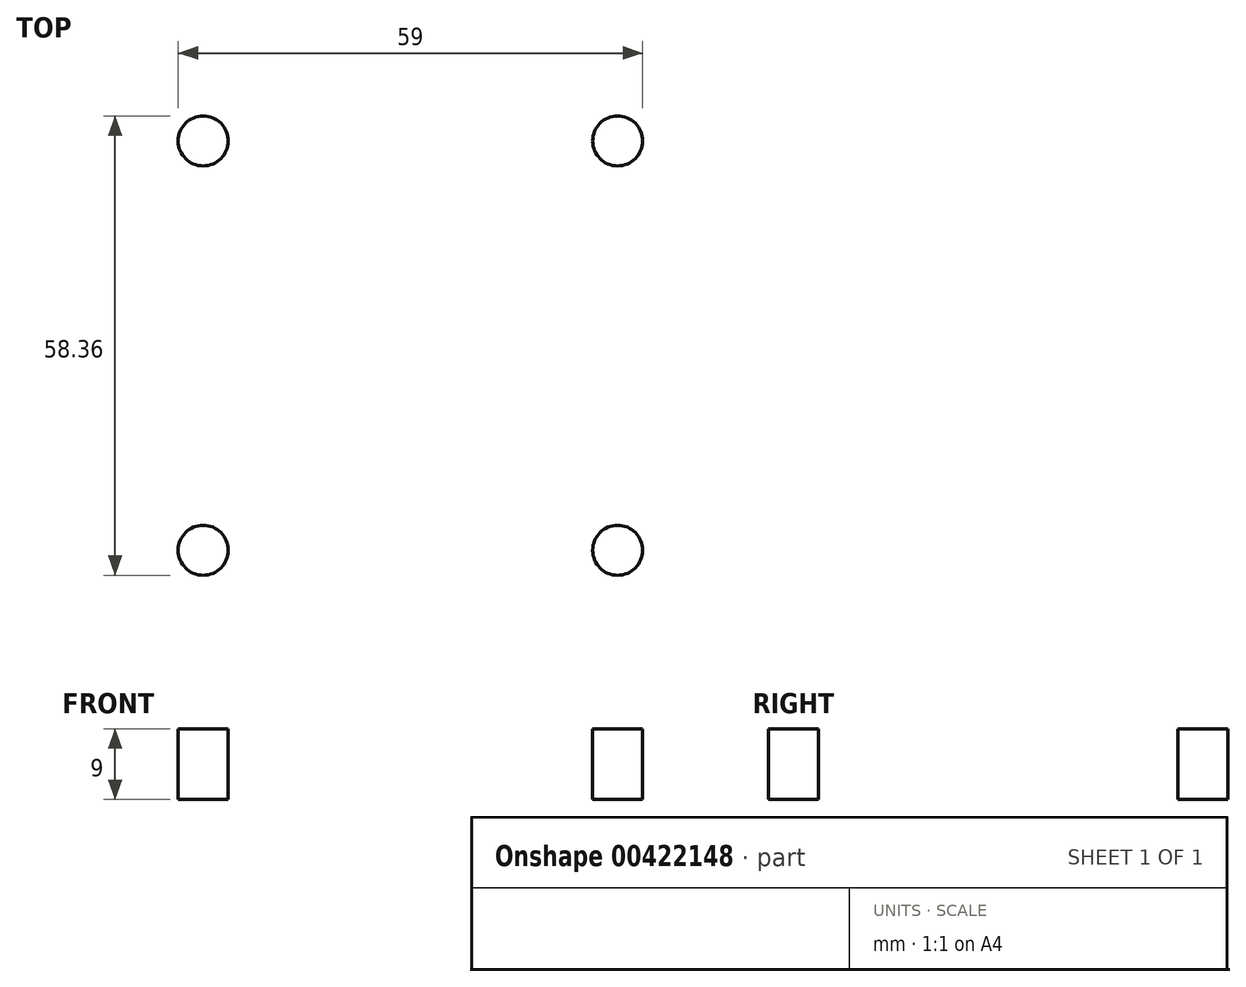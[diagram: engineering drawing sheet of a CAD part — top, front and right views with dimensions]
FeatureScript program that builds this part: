
annotation { "Feature Type Name" : "Feature", "Feature Type Description" : "" }
export const myFeature = defineFeature(function(context is Context, id is Id, definition is map)
    precondition{}
    {
        {
            var Q0;
            Q0=qCreatedBy(makeId("Top.planeOp"),FACE);
            var sketch = newSketch(context, id + "F0", { "sketchPlane" : qUnion([Q0])});
            skLineSegment(sketch, "E0", {"start": v(0, 60) * mm, "end": v(0, -60) * mm});
            skLineSegment(sketch, "E1", {"start": v(-70, 0) * mm, "end": v(70, 0) * mm});
            skLineSegment(sketch, "E2", {"start": v(-31, 37.5) * mm, "end": v(31, 37.5) * mm});
            skLineSegment(sketch, "E3", {"start": v(-31, -37.5) * mm, "end": v(31, -37.5) * mm});
            skCircle(sketch, "E4", {"center": v(-26.32, 26) * mm, "radius": 3.17 * mm});
            skCircle(sketch, "E5", {"center": v(-26.32, -26) * mm, "radius": 3.17 * mm});
            skCircle(sketch, "E6", {"center": v(26.32, -26) * mm, "radius": 3.17 * mm});
            skCircle(sketch, "E7", {"center": v(26.32, 26) * mm, "radius": 3.17 * mm});
            skCircle(sketch, "E8", {"center": v(-41, 0) * mm, "radius": 5.25 * mm});
            skCircle(sketch, "E9", {"center": v(41, 0) * mm, "radius": 5.25 * mm});
            skCircle(sketch, "E10", {"center": v(35, -11) * mm, "radius": 3.5 * mm});
            skLineSegment(sketch, "E11", {"start": v(-55, 12.5) * mm, "end": v(-55, -12.5) * mm});
            skLineSegment(sketch, "E12", {"start": v(55, 12.5) * mm, "end": v(55, -12.5) * mm});
            skCircle(sketch, "E13", {"center": v(0, 22.5) * mm, "radius": 3.17 * mm});
            skCircle(sketch, "E14", {"center": v(22.5, 0) * mm, "radius": 3.17 * mm});
            skCircle(sketch, "E15", {"center": v(0, -22.5) * mm, "radius": 3.17 * mm});
            skCircle(sketch, "E16", {"center": v(-22.5, 0) * mm, "radius": 3.17 * mm});
            skLineSegment(sketch, "E17", {"start": v(-40, 28.5) * mm, "end": v(-40, 27.5) * mm});
            skLineSegment(sketch, "E18", {"start": v(40, 28.5) * mm, "end": v(40, 27.5) * mm});
            skLineSegment(sketch, "E19", {"start": v(-40, -27.5) * mm, "end": v(-40, -28.5) * mm});
            skLineSegment(sketch, "E20", {"start": v(40, -27.5) * mm, "end": v(40, -28.5) * mm});
            skArc(sketch, "E21", {"start": v(-54, 13.5) * mm, "mid": v(-44.1, 17.6) * mm, "end": v(-40, 27.5) * mm});
            skArc(sketch, "E22", {"start": v(-40, -27.5) * mm, "mid": v(-44.1, -17.6) * mm, "end": v(-54, -13.5) * mm});
            skArc(sketch, "E23", {"start": v(54, -13.5) * mm, "mid": v(44.1, -17.6) * mm, "end": v(40, -27.5) * mm});
            skArc(sketch, "E24", {"start": v(40, 27.5) * mm, "mid": v(44.1, 17.6) * mm, "end": v(54, 13.5) * mm});
            skArc(sketch, "E25", {"start": v(-54, 13.5) * mm, "mid": v(-54.7, 13.2) * mm, "end": v(-55, 12.5) * mm});
            skArc(sketch, "E26", {"start": v(-55, -12.5) * mm, "mid": v(-54.7, -13.2) * mm, "end": v(-54, -13.5) * mm});
            skArc(sketch, "E27", {"start": v(55, 12.5) * mm, "mid": v(54.7, 13.2) * mm, "end": v(54, 13.5) * mm});
            skArc(sketch, "E28", {"start": v(54, -13.5) * mm, "mid": v(54.7, -13.2) * mm, "end": v(55, -12.5) * mm});
            skArc(sketch, "E29", {"start": v(-31, 37.5) * mm, "mid": v(-37.36, 34.86) * mm, "end": v(-40, 28.5) * mm});
            skArc(sketch, "E30", {"start": v(40, 28.5) * mm, "mid": v(37.36, 34.86) * mm, "end": v(31, 37.5) * mm});
            skArc(sketch, "E31", {"start": v(31, -37.5) * mm, "mid": v(37.36, -34.86) * mm, "end": v(40, -28.5) * mm});
            skArc(sketch, "E32", {"start": v(-40, -28.5) * mm, "mid": v(-37.36, -34.86) * mm, "end": v(-31, -37.5) * mm});
            skCircle(sketch, "E33", {"center": v(0, 0) * mm, "radius": 11.5 * mm});
            skSolve(sketch);
        }
        {
            var Q0;
            Q0=makeQuery(id+"F0.imprint","IMPRINT",FACE,{"disambiguationData":[TD([[makeQuery(id+"F0.imprint","IMPRINT",EDGE,{"derivedFrom":sQuery(id+"F0.wireOp",EDGE,"E4")}),1.0]])]});
            var Q1;
            Q1=makeQuery(id+"F0.imprint","IMPRINT",FACE,{"disambiguationData":[TD([[makeQuery(id+"F0.imprint","IMPRINT",EDGE,{"derivedFrom":sQuery(id+"F0.wireOp",EDGE,"E7")}),1.0]])]});
            var Q2;
            Q2=makeQuery(id+"F0.imprint","IMPRINT",FACE,{"disambiguationData":[TD([[makeQuery(id+"F0.imprint","IMPRINT",EDGE,{"derivedFrom":sQuery(id+"F0.wireOp",EDGE,"E6")}),1.0]])]});
            var Q3;
            Q3=makeQuery(id+"F0.imprint","IMPRINT",FACE,{"disambiguationData":[TD([[makeQuery(id+"F0.imprint","IMPRINT",EDGE,{"derivedFrom":sQuery(id+"F0.wireOp",EDGE,"E5")}),1.0]])]});
            extrude(context, id + "F1", {"entities" : qUnion([Q0, Q1, Q2, Q3]), "depth" : 9 * mm});
        }
    });
